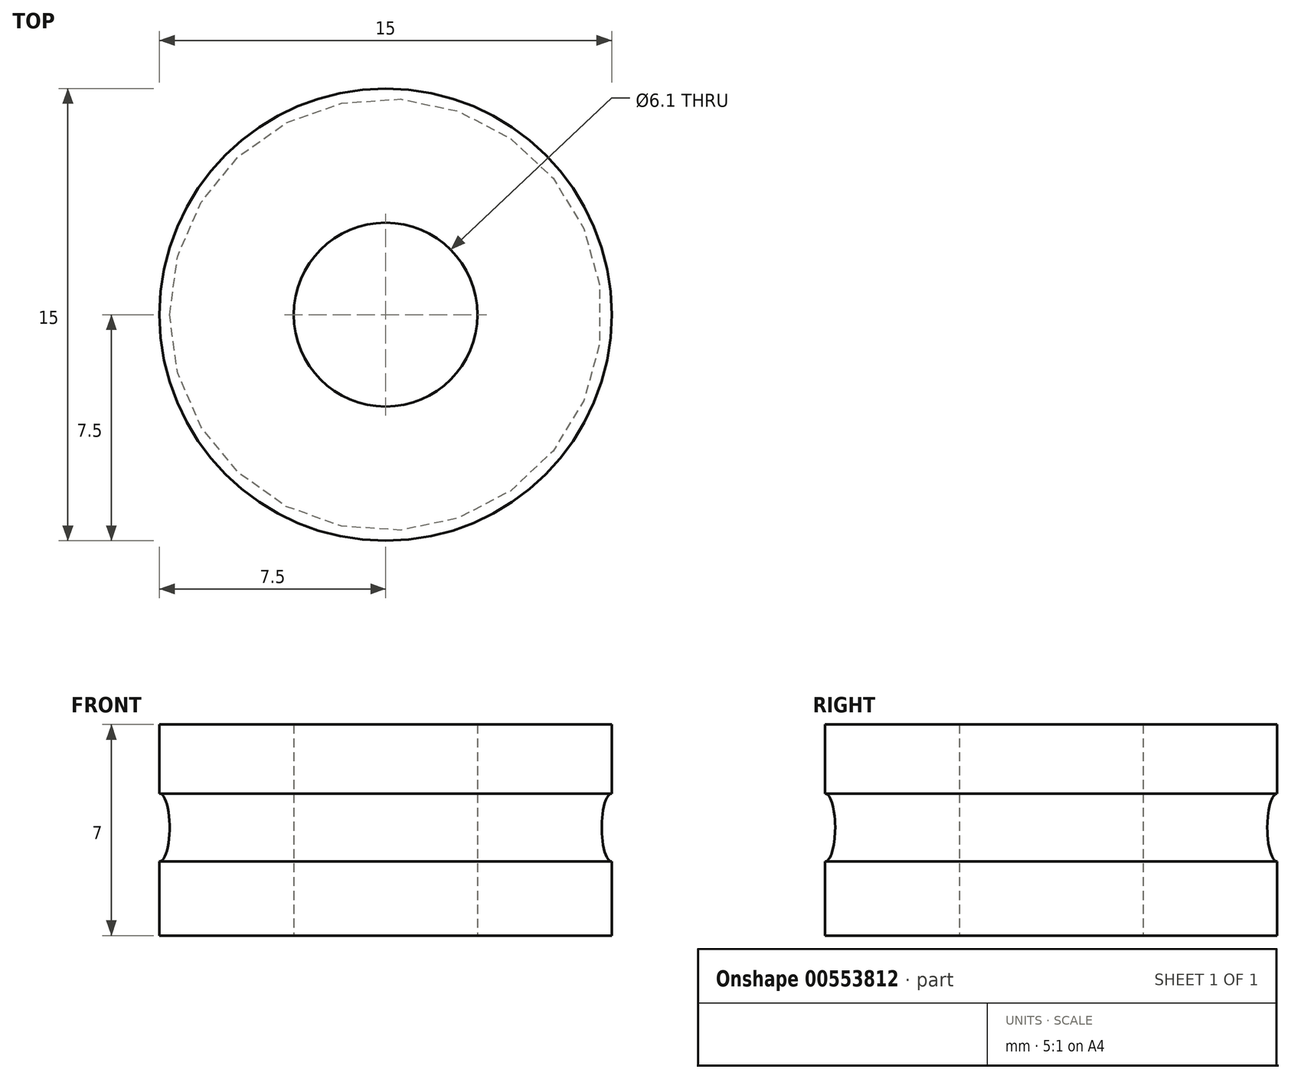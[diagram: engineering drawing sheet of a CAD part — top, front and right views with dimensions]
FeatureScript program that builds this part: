
annotation { "Feature Type Name" : "Feature", "Feature Type Description" : "" }
export const myFeature = defineFeature(function(context is Context, id is Id, definition is map)
    precondition{}
    {
        {
            var Q0;
            Q0=qCreatedBy(makeId("Top.planeOp"),FACE);
            var sketch = newSketch(context, id + "F0", { "sketchPlane" : qUnion([Q0])});
            skCircle(sketch, "E0", {"center": v(0, 0) * mm, "radius": 7.5 * mm});
            skCircle(sketch, "E1", {"center": v(0, 0) * mm, "radius": 3.05 * mm});
            skSolve(sketch);
        }
        {
            var Q0;
            Q0=qSketchRegion(id+"F0",true);
            extrude(context, id + "F1", {"entities" : qUnion([Q0]), "depth" : 7 * mm, "offsetDistance" : 25 * mm});
        }
        {
            var Q0;
            Q0=qCreatedBy(makeId("Front.planeOp"),FACE);
            var sketch = newSketch(context, id + "F2", { "sketchPlane" : qUnion([Q0])});
            skEllipse(sketch, "E2", {"center": v(7.5, 3.58) * mm, "majorRadius": 1.13 * mm, "minorRadius": 0.33 * mm, "majorAxis": v(0, -1)});
            skSolve(sketch);
        }
        {
            var Q0;
            Q0=makeQuery(id+"F2.imprint","IMPRINT",FACE,{"disambiguationData":[TD([[makeQuery(id+"F2.imprint","IMPRINT",EDGE,{"derivedFrom":sQuery(id+"F2.wireOp",EDGE,"E2")}),1.0]])]});
            var Q1;
            Q1=sQuery(id+"F2.wireOp",EDGE,"E2");
            var Q2;
            Q2=makeQuery(id+"F1.opExtrude","CAP_EDGE",EDGE,{"disambiguationData":[OSD([sQuery(id+"F0.wireOp",EDGE,"E1")])],"isStart":false});
            revolve(context, id + "F3", {"operationType" : NewBodyOperationType.REMOVE, "surfaceOperationType" : NewSurfaceOperationType.NEW, "entities" : qUnion([Q0]), "surfaceEntities" : qUnion([Q1]), "axis" : qUnion([Q2]), "revolveType" : RevolveType.FULL});
        }
    });
